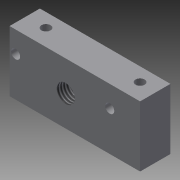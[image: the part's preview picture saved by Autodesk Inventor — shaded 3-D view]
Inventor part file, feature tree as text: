
AUTODESK INVENTOR PART (.ipt)
format: ipt  version: 2013 (Build 170138000, 138)  size: 116,736 bytes
history: native  units: mm
features: sketch x4, extrude x2, hole x2, thread x1
ambient origin geometry x8: Origin, YZ Plane, XZ Plane, XY Plane, X Axis, Y Axis, Z Axis, Center Point
bodies: Solid1 (feature_tree)
feature tree (9):
  extrude  "Extrusion1"  Depth=10.0mm
  extrude  "Extrusion2"  Depth=3.0mm
  hole  "Hole1"  [1 undecoded]
  hole  "Hole2"  [1 undecoded]
  thread  "Thread1"  [1 undecoded]
  sketch  "Sketch1"  dims[d0=43.0mm d1=10.0mm]
  sketch  "Sketch2"  dims[d2=3.0mm d3=3.0mm]
  sketch  "Sketch3"  dims[d4=6.5mm d5=31.0mm]
  sketch  "Sketch4"  dims[d6=4.5mm d7=20.0mm d8=0.0mm d9=7.0mm d10=2.0mm d11=3.0mm d12=3.0mm d13=31.0mm d14=20.0mm d15=0.0mm d16=6.0mm d18=10.0mm d19=18.5mm d20=6.0mm d21=6.0mm d22=4.0mm d23=2.0mm d24=90.0deg d25=0.0001mm d26=20.594885mm d27=10.0mm d28=18.5mm d29=6.0mm d30=6.0mm d31=4.0mm d32=2.0mm d33=90.0deg d34=8.0mm d35=135.0deg d36=10.0mm d37=0.0mm]
note: 3 required parameter values undecoded (feature->parameter linkage not recoverable at this tier; creation-order binding heuristic only, values carry confidence <= 0.55)
